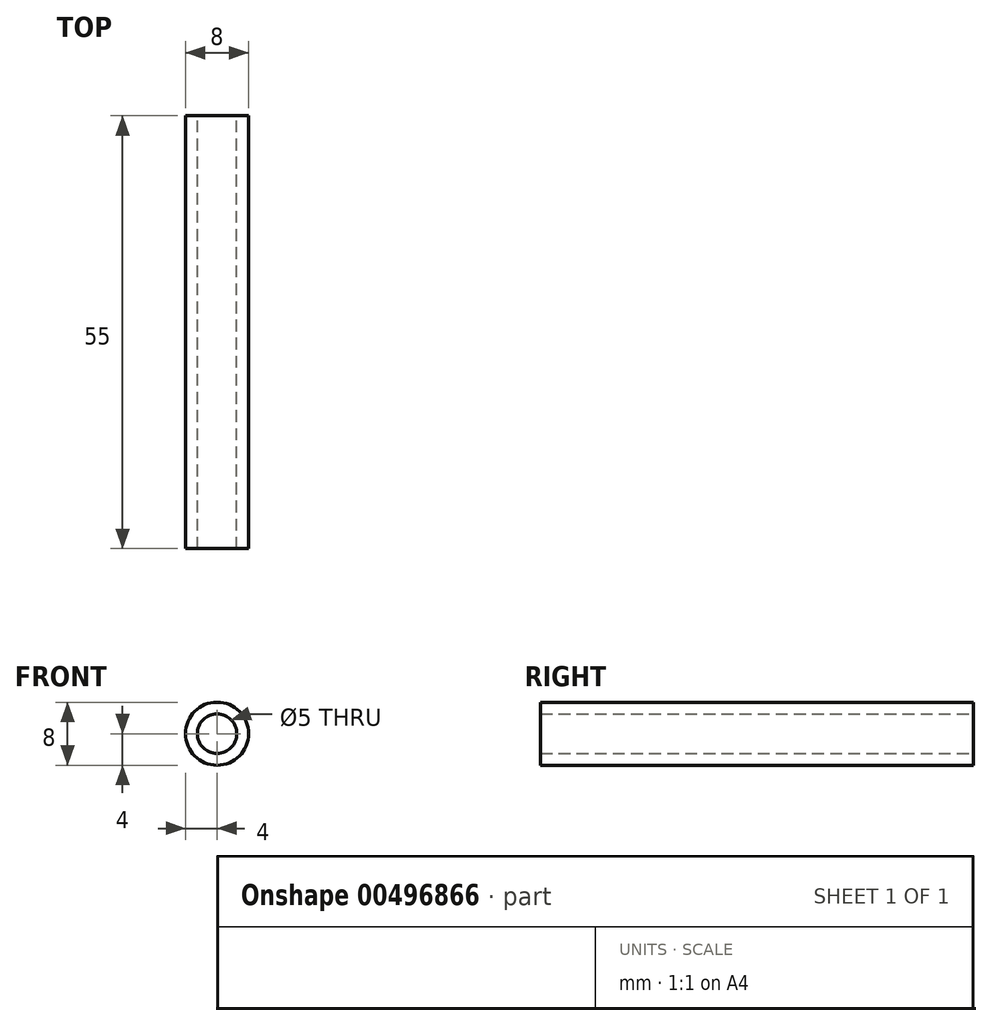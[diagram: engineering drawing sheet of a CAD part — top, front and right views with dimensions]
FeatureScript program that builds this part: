
annotation { "Feature Type Name" : "Feature", "Feature Type Description" : "" }
export const myFeature = defineFeature(function(context is Context, id is Id, definition is map)
    precondition{}
    {
        {
            var Q0;
            Q0=qCreatedBy(makeId("Front.planeOp"),FACE);
            var sketch = newSketch(context, id + "F0", { "sketchPlane" : qUnion([Q0])});
            skCircle(sketch, "E0", {"center": v(0, 0) * mm, "radius": 4 * mm});
            skCircle(sketch, "E1", {"center": v(0, 0) * mm, "radius": 2.5 * mm});
            skSolve(sketch);
        }
        {
            var Q0;
            Q0 = qSketchRegion(id + "F0", true);
            extrude(context, id + "F1", {"entities" : qUnion([Q0]), "depth" : 55 * mm, "offsetDistance" : 25 * mm});
        }
    });
